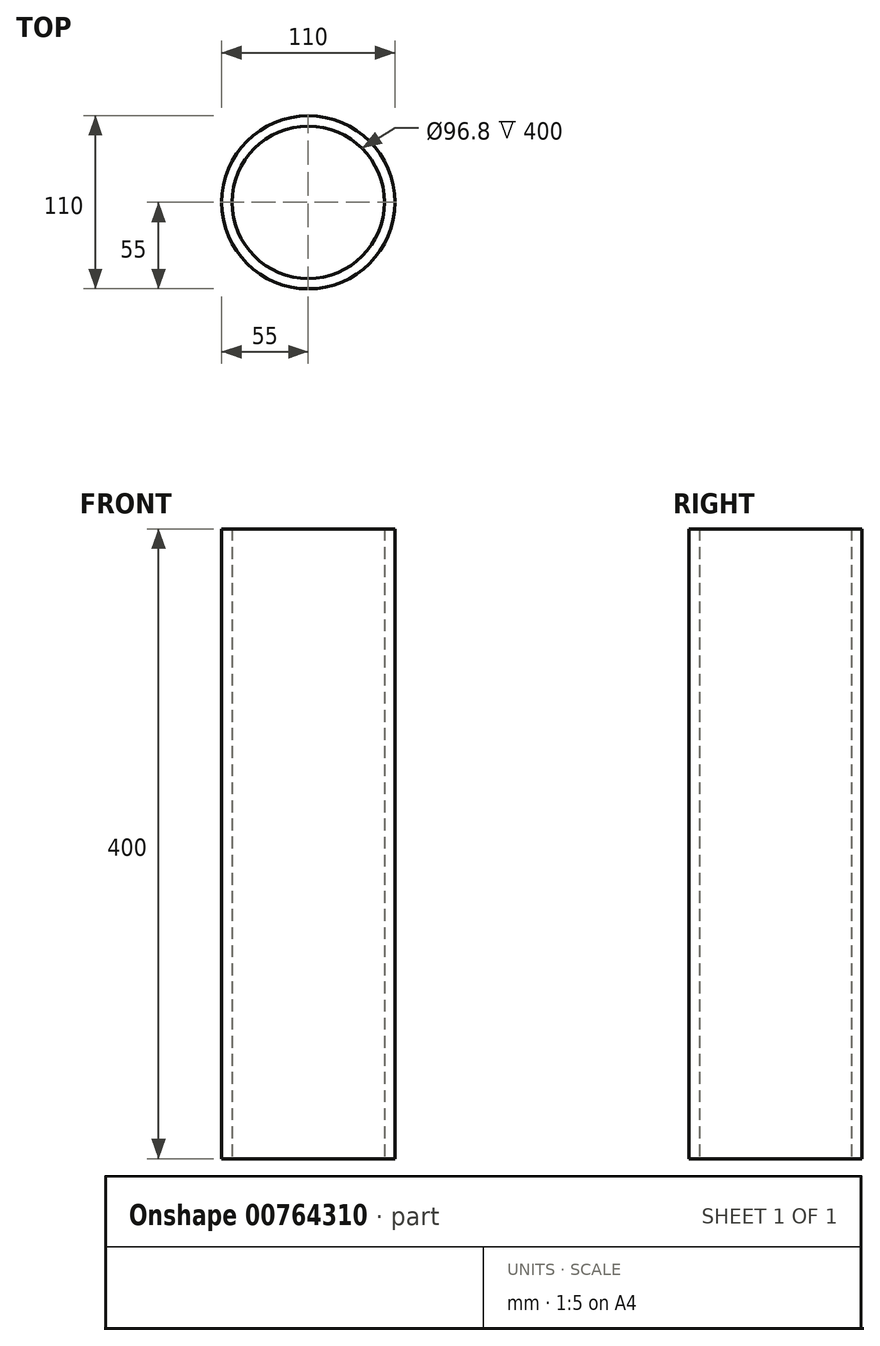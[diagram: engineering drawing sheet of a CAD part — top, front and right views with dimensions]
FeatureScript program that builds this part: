
annotation { "Feature Type Name" : "Feature", "Feature Type Description" : "" }
export const myFeature = defineFeature(function(context is Context, id is Id, definition is map)
    precondition{}
    {
        {
            var Q0;
            Q0=qCreatedBy(makeId("Top.planeOp"),FACE);
            var sketch = newSketch(context, id + "F0", { "sketchPlane" : qUnion([Q0])});
            skCircle(sketch, "E0", {"center": v(0, 0) * mm, "radius": 48.4 * mm});
            skCircle(sketch, "E1", {"center": v(0, 0) * mm, "radius": 55 * mm});
            skSolve(sketch);
        }
        {
            var Q0;
            Q0=makeQuery(id+"F0.imprint","IMPRINT",FACE,{"disambiguationData":[TD([[makeQuery(id+"F0.imprint","IMPRINT",EDGE,{"derivedFrom":sQuery(id+"F0.wireOp",EDGE,"E0")}),-1.0]])]});
            extrude(context, id + "F1", {"entities" : qUnion([Q0]), "depth" : 400 * mm, "offsetDistance" : 25 * mm});
        }
    });
